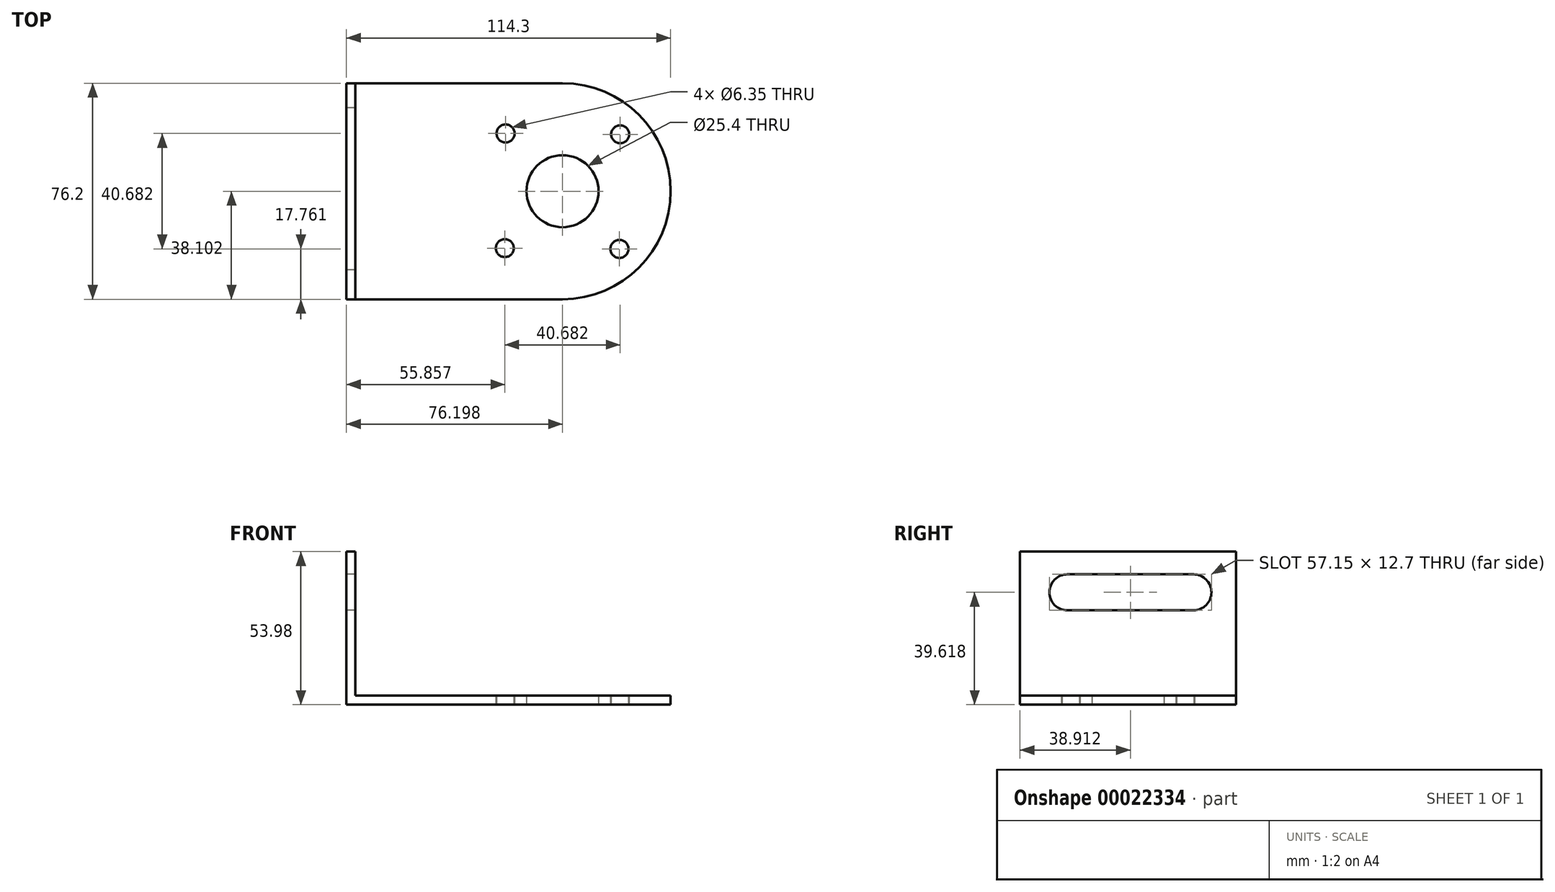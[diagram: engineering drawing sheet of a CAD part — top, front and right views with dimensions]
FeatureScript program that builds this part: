
annotation { "Feature Type Name" : "Feature", "Feature Type Description" : "" }
export const myFeature = defineFeature(function(context is Context, id is Id, definition is map)
    precondition{}
    {
        {
            var Q0;
            Q0=qCreatedBy(makeId("Top.planeOp"),FACE);
            var sketch = newSketch(context, id + "F0", { "sketchPlane" : qUnion([Q0])});
            skLineSegment(sketch, "E0.bottom", {"start": v(-49, 29.88) * mm, "end": v(27.2, 29.88) * mm});
            skLineSegment(sketch, "E0.top", {"start": v(-49, -46.32) * mm, "end": v(27.2, -46.32) * mm});
            skLineSegment(sketch, "E0.left", {"start": v(-49, 29.88) * mm, "end": v(-49, -46.32) * mm});
            skLineSegment(sketch, "E0.right", {"start": v(27.2, 29.88) * mm, "end": v(27.2, -46.32) * mm});
            skCircle(sketch, "E1", {"center": v(27.2, -8.22) * mm, "radius": 38.1 * mm});
            skCircle(sketch, "E2", {"center": v(27.2, -8.22) * mm, "radius": 12.7 * mm});
            skCircle(sketch, "E3", {"center": v(7.14, 12.12) * mm, "radius": 3.18 * mm});
            skCircle(sketch, "E4.1.0", {"center": v(6.87, -28.29) * mm, "radius": 3.18 * mm});
            skCircle(sketch, "E4.2.0", {"center": v(47.28, -28.56) * mm, "radius": 3.18 * mm});
            skCircle(sketch, "E4.3.0", {"center": v(47.55, 11.85) * mm, "radius": 3.18 * mm});
            skSolve(sketch);
        }
        {
            var Q0;
            Q0 = qSketchRegion(id + "F0", true);
            extrude(context, id + "F1", {"entities" : qUnion([Q0]), "depth" : 3.17 * mm});
        }
        {
            var Q0;
            Q0=makeQuery(id+"F1.opExtrude","CAP_FACE",FACE,{"disambiguationData":[OSD([sQuery(id+"F0.wireOp",EDGE,"E0.bottom"),sQuery(id+"F0.wireOp",EDGE,"E0.top"),sQuery(id+"F0.wireOp",EDGE,"E0.left"),sQuery(id+"F0.wireOp",EDGE,"E1"),sQuery(id+"F0.wireOp",EDGE,"E2"),sQuery(id+"F0.wireOp",EDGE,"E3"),sQuery(id+"F0.wireOp",EDGE,"E4.1.0"),sQuery(id+"F0.wireOp",EDGE,"E4.2.0"),sQuery(id+"F0.wireOp",EDGE,"E4.3.0")])],"isStart":false});
            var sketch = newSketch(context, id + "F2", { "sketchPlane" : qUnion([Q0])});
            skLineSegment(sketch, "E5.bottom", {"start": v(-49, 29.88) * mm, "end": v(-45.82, 29.88) * mm});
            skLineSegment(sketch, "E5.top", {"start": v(-49, -46.32) * mm, "end": v(-45.82, -46.32) * mm});
            skLineSegment(sketch, "E5.left", {"start": v(-49, 29.88) * mm, "end": v(-49, -46.32) * mm});
            skLineSegment(sketch, "E5.right", {"start": v(-45.82, 29.88) * mm, "end": v(-45.82, -46.32) * mm});
            skSolve(sketch);
        }
        {
            var Q0;
            Q0 = qSketchRegion(id + "F2", true);
            extrude(context, id + "F3", {"entities" : qUnion([Q0]), "operationType" : NewBodyOperationType.ADD, "depth" : 53.97 * mm});
        }
        {
            var Q0;
            Q0=makeQuery(id+"F3.boolean.opBoolean","MERGE",FACE,{"derivedFrom":[makeQuery(id+"F1.opExtrude","SWEPT_FACE",FACE,{"disambiguationData":[OSD([sQuery(id+"F0.wireOp",EDGE,"E0.left")])]}),makeQuery(id+"F3.opExtrude","SWEPT_FACE",FACE,{"disambiguationData":[OSD([sQuery(id+"F2.wireOp",EDGE,"E5.left")])]})]});
            var sketch = newSketch(context, id + "F4", { "sketchPlane" : qUnion([Q0])});
            skLineSegment(sketch, "E6", {"start": v(-14.82, 45.97) * mm, "end": v(29.23, 45.97) * mm});
            skLineSegment(sketch, "E7.bottom", {"start": v(-14.82, 45.97) * mm, "end": v(29.63, 45.97) * mm});
            skLineSegment(sketch, "E7.top", {"start": v(-14.82, 33.27) * mm, "end": v(29.63, 33.27) * mm});
            skLineSegment(sketch, "E7.left", {"start": v(-14.82, 45.97) * mm, "end": v(-14.82, 33.27) * mm});
            skLineSegment(sketch, "E7.right", {"start": v(29.63, 45.97) * mm, "end": v(29.63, 33.27) * mm});
            skLineSegment(sketch, "E8", {"start": v(-14.82, 39.62) * mm, "end": v(29.63, 39.62) * mm, "construction": true});
            skCircle(sketch, "E9", {"center": v(-14.82, 39.62) * mm, "radius": 6.35 * mm, "construction": true});
            skCircle(sketch, "E10", {"center": v(29.63, 39.62) * mm, "radius": 6.35 * mm, "construction": true});
            skCircle(sketch, "E11", {"center": v(-14.82, 39.62) * mm, "radius": 6.35 * mm});
            skCircle(sketch, "E12", {"center": v(29.63, 39.62) * mm, "radius": 6.35 * mm});
            skSolve(sketch);
        }
        {
            var Q0;
            Q0 = qSketchRegion(id + "F4", true);
            var Q1;
            {var subQ1=sQuery(id+"F4.wireOp",EDGE,"E7.right");Q1=makeQuery(id+"F4.imprint","IMPRINT",FACE,{"disambiguationData":[TD([[makeQuery(id+"F4.imprint","IMPRINT",EDGE,{"derivedFrom":subQ1}),-1.0]])]});}
            extrude(context, id + "F5", {"entities" : qUnion([Q0, Q1]), "operationType" : NewBodyOperationType.REMOVE, "endBound" : BoundingType.UP_TO_NEXT, "oppositeDirection" : true, "depth" : 25.4 * mm});
        }
        {
            var Q0;
            Q0=makeQuery(id+"F3.opExtrude","CAP_FACE",FACE,{"disambiguationData":[OSD([sQuery(id+"F2.wireOp",EDGE,"E5.bottom"),sQuery(id+"F2.wireOp",EDGE,"E5.top"),sQuery(id+"F2.wireOp",EDGE,"E5.left"),sQuery(id+"F2.wireOp",EDGE,"E5.right")])],"isStart":false});
            extrude(context, id + "F6", {"entities" : qUnion([Q0]), "operationType" : NewBodyOperationType.REMOVE, "oppositeDirection" : true, "depth" : 3.17 * mm});
        }
    });
